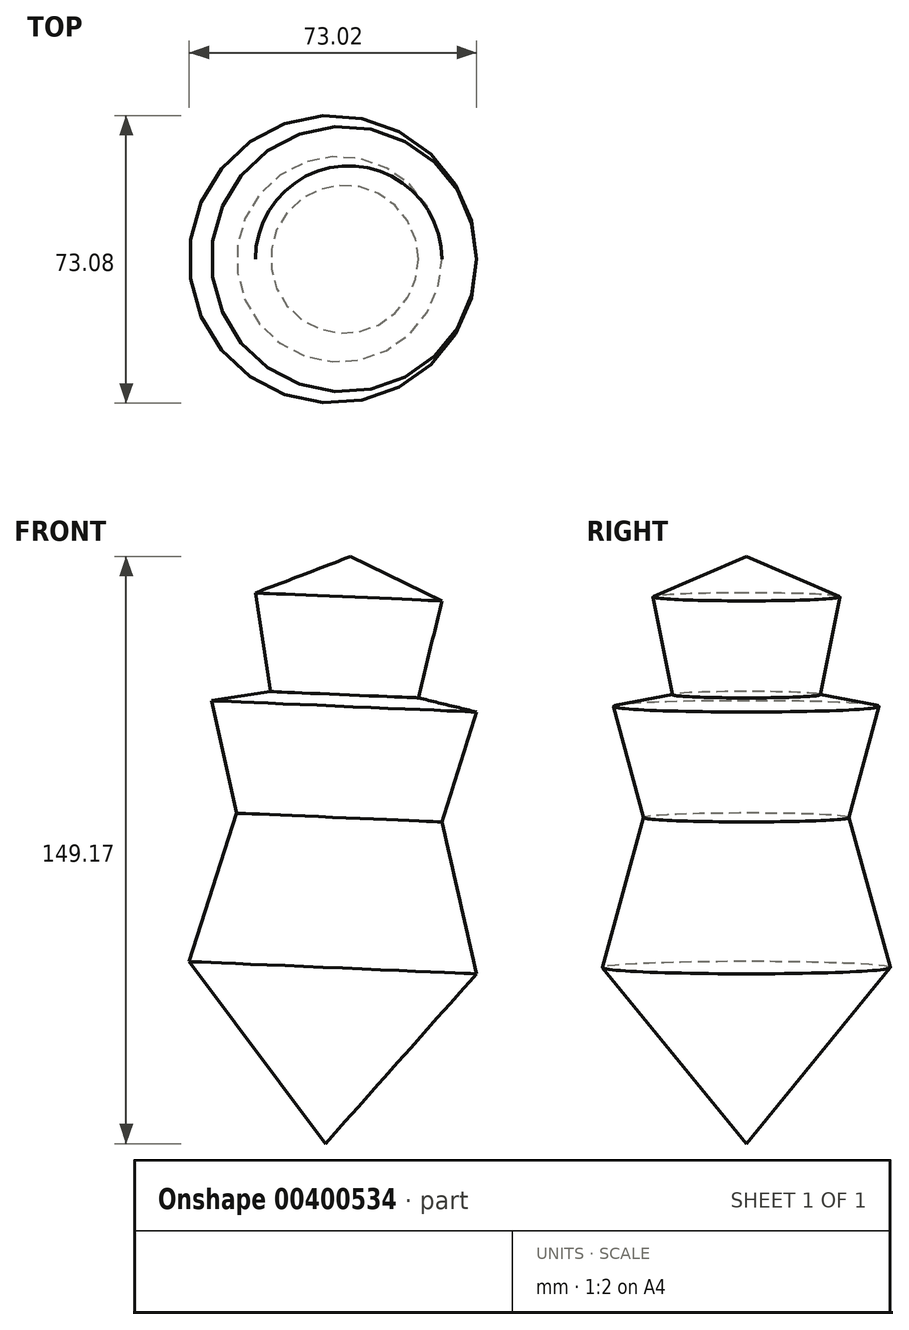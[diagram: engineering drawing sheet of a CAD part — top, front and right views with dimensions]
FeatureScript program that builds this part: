
annotation { "Feature Type Name" : "Feature", "Feature Type Description" : "" }
export const myFeature = defineFeature(function(context is Context, id is Id, definition is map)
    precondition{}
    {
        {
            var Q0;
            Q0=qCreatedBy(makeId("Front.planeOp"),FACE);
            var sketch = newSketch(context, id + "F0", { "sketchPlane" : qUnion([Q0])});
            skLineSegment(sketch, "E0", {"start": v(-13.75, 73.93) * mm, "end": v(-20.1, -75.24) * mm});
            skLineSegment(sketch, "E1", {"start": v(-13.75, 73.93) * mm, "end": v(9.52, 62.67) * mm});
            skLineSegment(sketch, "E2", {"start": v(9.52, 62.67) * mm, "end": v(3.52, 38.03) * mm});
            skLineSegment(sketch, "E3", {"start": v(3.52, 38.03) * mm, "end": v(18.32, 34.43) * mm});
            skLineSegment(sketch, "E4", {"start": v(9.52, 6.52) * mm, "end": v(18.32, 34.43) * mm});
            skLineSegment(sketch, "E5", {"start": v(9.52, 6.52) * mm, "end": v(18.32, -32.08) * mm});
            skLineSegment(sketch, "E6", {"start": v(18.32, -32.08) * mm, "end": v(-20.1, -75.24) * mm});
            skSolve(sketch);
        }
        {
            var Q0;
            Q0=makeQuery(id+"F0.imprint","IMPRINT",FACE,{"disambiguationData":[TD([[makeQuery(id+"F0.imprint","IMPRINT",EDGE,{"derivedFrom":sQuery(id+"F0.wireOp",EDGE,"E0")}),1.0]])]});
            var Q1;
            Q1=sQuery(id+"F0.wireOp",EDGE,"E0");
            revolve(context, id + "F1", {"entities" : qUnion([Q0]), "axis" : qUnion([Q1]), "revolveType" : RevolveType.FULL});
        }
    });
